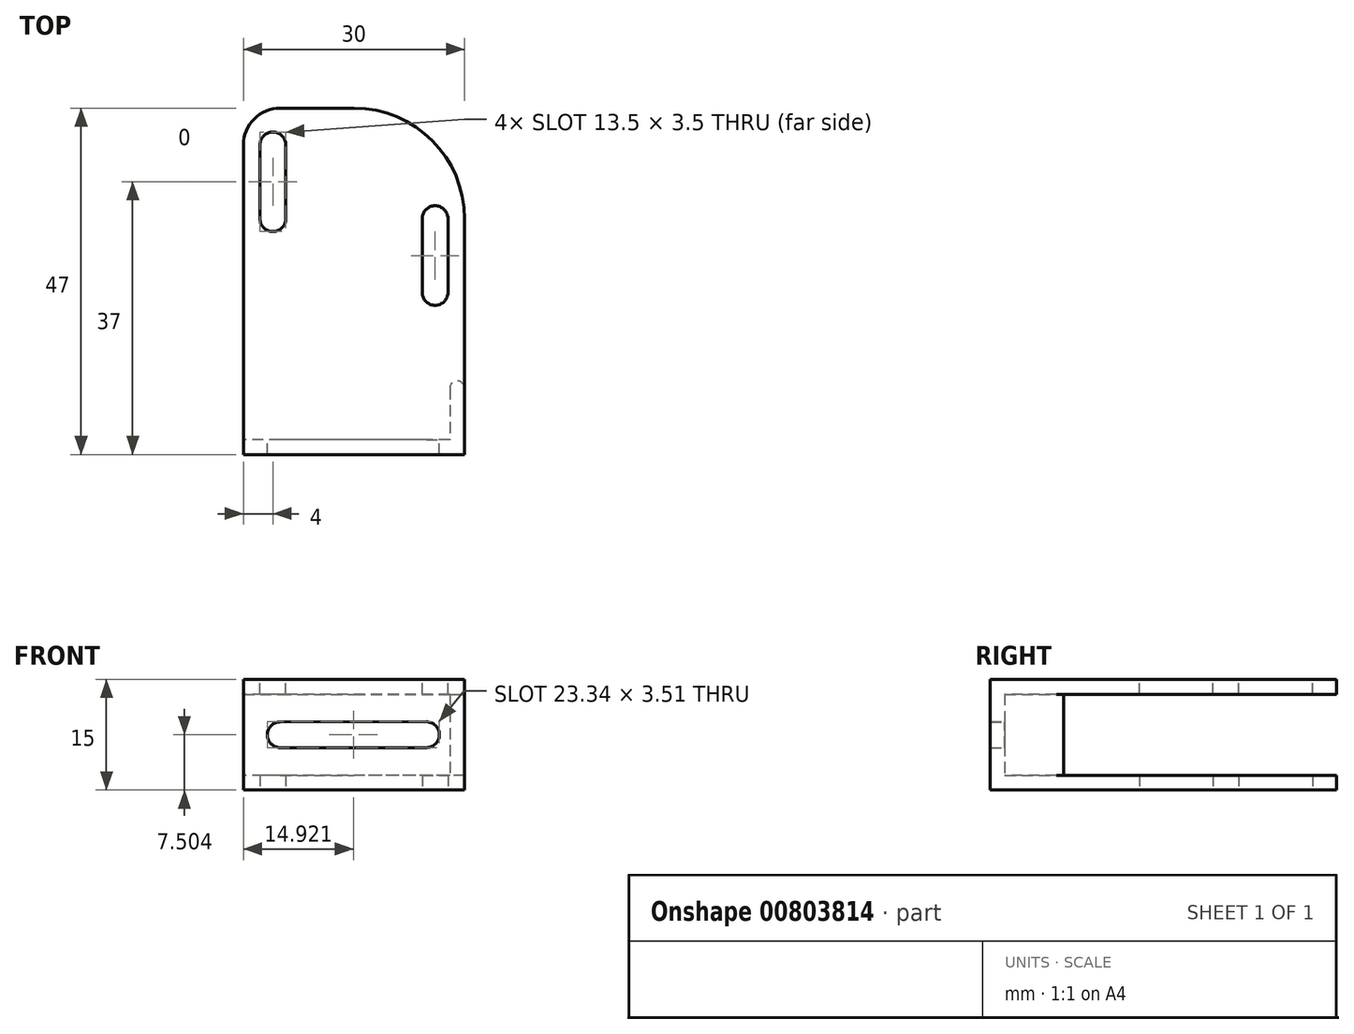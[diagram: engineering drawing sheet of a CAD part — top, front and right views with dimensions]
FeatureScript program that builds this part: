
annotation { "Feature Type Name" : "Feature", "Feature Type Description" : "" }
export const myFeature = defineFeature(function(context is Context, id is Id, definition is map)
    precondition{}
    {
        {
            var Q0;
            Q0=qCreatedBy(makeId("Top.planeOp"),FACE);
            var sketch = newSketch(context, id + "F0", { "sketchPlane" : qUnion([Q0])});
            skLineSegment(sketch, "E0", {"start": v(0, 0) * mm, "end": v(0, -45) * mm});
            skLineSegment(sketch, "E1", {"start": v(0, -45) * mm, "end": v(-30, -45) * mm});
            skLineSegment(sketch, "E2", {"start": v(-30, -45) * mm, "end": v(-30, 0) * mm});
            skLineSegment(sketch, "E3", {"start": v(-30, 0) * mm, "end": v(0, 0) * mm});
            skLineSegment(sketch, "E4", {"start": v(-15, 0) * mm, "end": v(-15, -45) * mm, "construction": true});
            skCircle(sketch, "E5", {"center": v(-4, -25) * mm, "radius": 1.75 * mm});
            skCircle(sketch, "E6", {"center": v(-26, -5) * mm, "radius": 1.75 * mm});
            skCircle(sketch, "E7", {"center": v(-26, -15) * mm, "radius": 1.75 * mm});
            skCircle(sketch, "E8", {"center": v(-4, -15) * mm, "radius": 1.75 * mm});
            skLineSegment(sketch, "E9", {"start": v(-5.75, -15) * mm, "end": v(-5.75, -25) * mm});
            skLineSegment(sketch, "E10", {"start": v(-2.25, -15) * mm, "end": v(-2.25, -25) * mm});
            skLineSegment(sketch, "E11", {"start": v(-24.25, -5) * mm, "end": v(-24.25, -15) * mm});
            skLineSegment(sketch, "E12", {"start": v(-27.75, -5) * mm, "end": v(-27.75, -15) * mm});
            skSolve(sketch);
        }
        {
            var Q0;
            Q0=makeQuery(id+"F0.imprint","IMPRINT",FACE,{"disambiguationData":[TD([[makeQuery(id+"F0.imprint","IMPRINT",EDGE,{"derivedFrom":sQuery(id+"F0.wireOp",EDGE,"E0")}),-1.0]])]});
            extrude(context, id + "F1", {"entities" : qUnion([Q0]), "depth" : 2 * mm, "offsetDistance" : 25 * mm});
        }
        {
            var Q0;
            Q0=makeQuery(id+"F1.opExtrude","SWEPT_FACE",FACE,{"disambiguationData":[OSD([sQuery(id+"F0.wireOp",EDGE,"E1")])]});
            var sketch = newSketch(context, id + "F2", { "sketchPlane" : qUnion([Q0])});
            skLineSegment(sketch, "E13", {"start": v(-30, 0) * mm, "end": v(-30, 7.5) * mm});
            skLineSegment(sketch, "E14", {"start": v(-30, 7.5) * mm, "end": v(0, 7.5) * mm});
            skLineSegment(sketch, "E15", {"start": v(0, 7.5) * mm, "end": v(0, 0) * mm});
            skLineSegment(sketch, "E16", {"start": v(0, 0) * mm, "end": v(-30, 0) * mm});
            skSolve(sketch);
        }
        {
            var Q0;
            {var subQ0=sQuery(id+"F2.wireOp",EDGE,"E16");Q0=makeQuery(id+"F2.imprint","IMPRINT",FACE,{"disambiguationData":[TD([[makeQuery(id+"F2.imprint","IMPRINT",EDGE,{"derivedFrom":subQ0}),-1.0]])]});}
            var Q1;
            {var subQ2=sQuery(id+"F2.wireOp",EDGE,"E14");Q1=makeQuery(id+"F2.imprint","IMPRINT",FACE,{"disambiguationData":[TD([[makeQuery(id+"F2.imprint","IMPRINT",EDGE,{"derivedFrom":subQ2}),-1.0]])]});}
            extrude(context, id + "F3", {"entities" : qUnion([Q0, Q1]), "operationType" : NewBodyOperationType.ADD, "depth" : 2 * mm, "offsetDistance" : 25 * mm});
        }
        {
            var Q0;
            Q0=makeQuery(id+"F1.opExtrude","SWEPT_BODY",BODY,{"disambiguationData":[OSD([sQuery(id+"F0.wireOp",EDGE,"E0"),sQuery(id+"F0.wireOp",EDGE,"E1"),sQuery(id+"F0.wireOp",EDGE,"E2"),sQuery(id+"F0.wireOp",EDGE,"E3"),sQuery(id+"F0.wireOp",EDGE,"E5"),sQuery(id+"F0.wireOp",EDGE,"E6"),sQuery(id+"F0.wireOp",EDGE,"E7"),sQuery(id+"F0.wireOp",EDGE,"E8"),sQuery(id+"F0.wireOp",EDGE,"E9"),sQuery(id+"F0.wireOp",EDGE,"E10"),sQuery(id+"F0.wireOp",EDGE,"E11"),sQuery(id+"F0.wireOp",EDGE,"E12")])]});
            var Q1;
            Q1=makeQuery(id+"F3.opExtrude","SWEPT_FACE",FACE,{"disambiguationData":[OSD([sQuery(id+"F2.wireOp",EDGE,"E14")])]});
            mirror(context, id + "F4", {"operationType" : NewBodyOperationType.ADD, "entities" : qUnion([Q0]), "mirrorPlane" : qUnion([Q1])});
        }
        {
            var Q0;
            {var subQ0=makeQuery(id+"F3.opExtrude","CAP_FACE",FACE,{"disambiguationData":[OSD([sQuery(id+"F2.wireOp",EDGE,"E13"),sQuery(id+"F2.wireOp",EDGE,"E14"),sQuery(id+"F2.wireOp",EDGE,"E15"),sQuery(id+"F2.wireOp",EDGE,"E16")])],"isStart":true});Q0=makeQuery(id+"F4.boolean.opBoolean","MERGE",FACE,{"derivedFrom":[subQ0,makeQuery(id+"F4.opPattern","COPY",FACE,{"derivedFrom":subQ0,"instanceName":"1"})]});}
            var sketch = newSketch(context, id + "F5", { "sketchPlane" : qUnion([Q0])});
            skLineSegment(sketch, "E17", {"start": v(0, 7.5) * mm, "end": v(30, 7.5) * mm, "construction": true});
            skLineSegment(sketch, "E18", {"start": v(5.16, 5.76) * mm, "end": v(25, 5.75) * mm});
            skLineSegment(sketch, "E19", {"start": v(5.16, 9.26) * mm, "end": v(25, 9.25) * mm});
            skArc(sketch, "E20", {"start": v(5.16, 9.26) * mm, "mid": v(3.4, 7.5) * mm, "end": v(5.16, 5.76) * mm});
            skArc(sketch, "E21", {"start": v(25, 5.75) * mm, "mid": v(26.75, 7.5) * mm, "end": v(25, 9.25) * mm});
            skSolve(sketch);
        }
        {
            var Q0;
            Q0 = qSketchRegion(id + "F5", true);
            extrude(context, id + "F6", {"entities" : qUnion([Q0]), "operationType" : NewBodyOperationType.REMOVE, "oppositeDirection" : true, "depth" : 25 * mm, "offsetDistance" : 25 * mm});
        }
        {
            var Q0;
            {var subQ0=makeQuery(id+"F3.boolean.opBoolean","MERGE",FACE,{"derivedFrom":[makeQuery(id+"F1.opExtrude","SWEPT_FACE",FACE,{"disambiguationData":[OSD([sQuery(id+"F0.wireOp",EDGE,"E0")])]}),makeQuery(id+"F3.opExtrude","SWEPT_FACE",FACE,{"disambiguationData":[OSD([sQuery(id+"F2.wireOp",EDGE,"E15")])]})]});Q0=makeQuery(id+"F4.boolean.opBoolean","MERGE",FACE,{"derivedFrom":[subQ0,makeQuery(id+"F4.opPattern","COPY",FACE,{"derivedFrom":subQ0,"instanceName":"1"})]});}
            var sketch = newSketch(context, id + "F7", { "sketchPlane" : qUnion([Q0])});
            skLineSegment(sketch, "E22", {"start": v(-37, 15) * mm, "end": v(-37, 0) * mm});
            skSolve(sketch);
        }
        {
            var Q0;
            {var subQ5=makeQuery(id+"F3.opExtrude","CAP_EDGE",EDGE,{"disambiguationData":[OSD([sQuery(id+"F2.wireOp",EDGE,"E15")])],"isStart":true});var subQ6=makeQuery(id+"F4.boolean.opBoolean","MERGE",EDGE,{"derivedFrom":[subQ5,makeQuery(id+"F4.opPattern","COPY",EDGE,{"derivedFrom":subQ5,"instanceName":"1"})]});Q0=makeQuery(id+"F7.imprint","IMPRINT",FACE,{"disambiguationData":[TD([[makeQuery(id+"F7.imprint","IMPRINT",EDGE,{"derivedFrom":subQ6}),1.0]])]});}
            extrude(context, id + "F8", {"entities" : qUnion([Q0]), "operationType" : NewBodyOperationType.ADD, "oppositeDirection" : true, "depth" : 2 * mm, "offsetDistance" : 25 * mm});
        }
        {
            var Q0;
            Q0=makeQuery(id+"F1.opExtrude","SWEPT_EDGE",EDGE,{"disambiguationData":[OSD([sQuery(id+"F0.wireOp",EDGE,"E0"),sQuery(id+"F0.wireOp",EDGE,"E3")])]});
            var Q1;
            Q1=makeQuery(id+"F4.opPattern","COPY",EDGE,{"derivedFrom":makeQuery(id+"F1.opExtrude","SWEPT_EDGE",EDGE,{"disambiguationData":[OSD([sQuery(id+"F0.wireOp",EDGE,"E0"),sQuery(id+"F0.wireOp",EDGE,"E3")])]}),"instanceName":"1"});
            fillet(context, id + "F9", {"entities" : qUnion([Q0, Q1]), "radius" : 15 * mm, "tangentPropagation" : true, "allowEdgeOverflow" : false});
        }
        {
            var Q0;
            Q0=makeQuery(id+"F4.opPattern","COPY",EDGE,{"derivedFrom":makeQuery(id+"F1.opExtrude","SWEPT_EDGE",EDGE,{"disambiguationData":[OSD([sQuery(id+"F0.wireOp",EDGE,"E2"),sQuery(id+"F0.wireOp",EDGE,"E3")])]}),"instanceName":"1"});
            var Q1;
            Q1=makeQuery(id+"F1.opExtrude","SWEPT_EDGE",EDGE,{"disambiguationData":[OSD([sQuery(id+"F0.wireOp",EDGE,"E2"),sQuery(id+"F0.wireOp",EDGE,"E3")])]});
            fillet(context, id + "F10", {"entities" : qUnion([Q0, Q1]), "radius" : 5 * mm, "tangentPropagation" : true, "allowEdgeOverflow" : false});
        }
        {
            var Q0;
            Q0=makeQuery(id+"F8.opExtrude","CAP_EDGE",EDGE,{"disambiguationData":[OSD([sQuery(id+"F7.wireOp",EDGE,"E22")])],"isStart":false});
            var Q1;
            Q1=makeQuery(id+"F8.opExtrude","CAP_EDGE",EDGE,{"disambiguationData":[OSD([sQuery(id+"F7.wireOp",EDGE,"E22")])],"isStart":true});
            fillet(context, id + "F11", {"entities" : qUnion([Q0, Q1]), "radius" : 1 * mm, "tangentPropagation" : true, "allowEdgeOverflow" : false});
        }
    });
